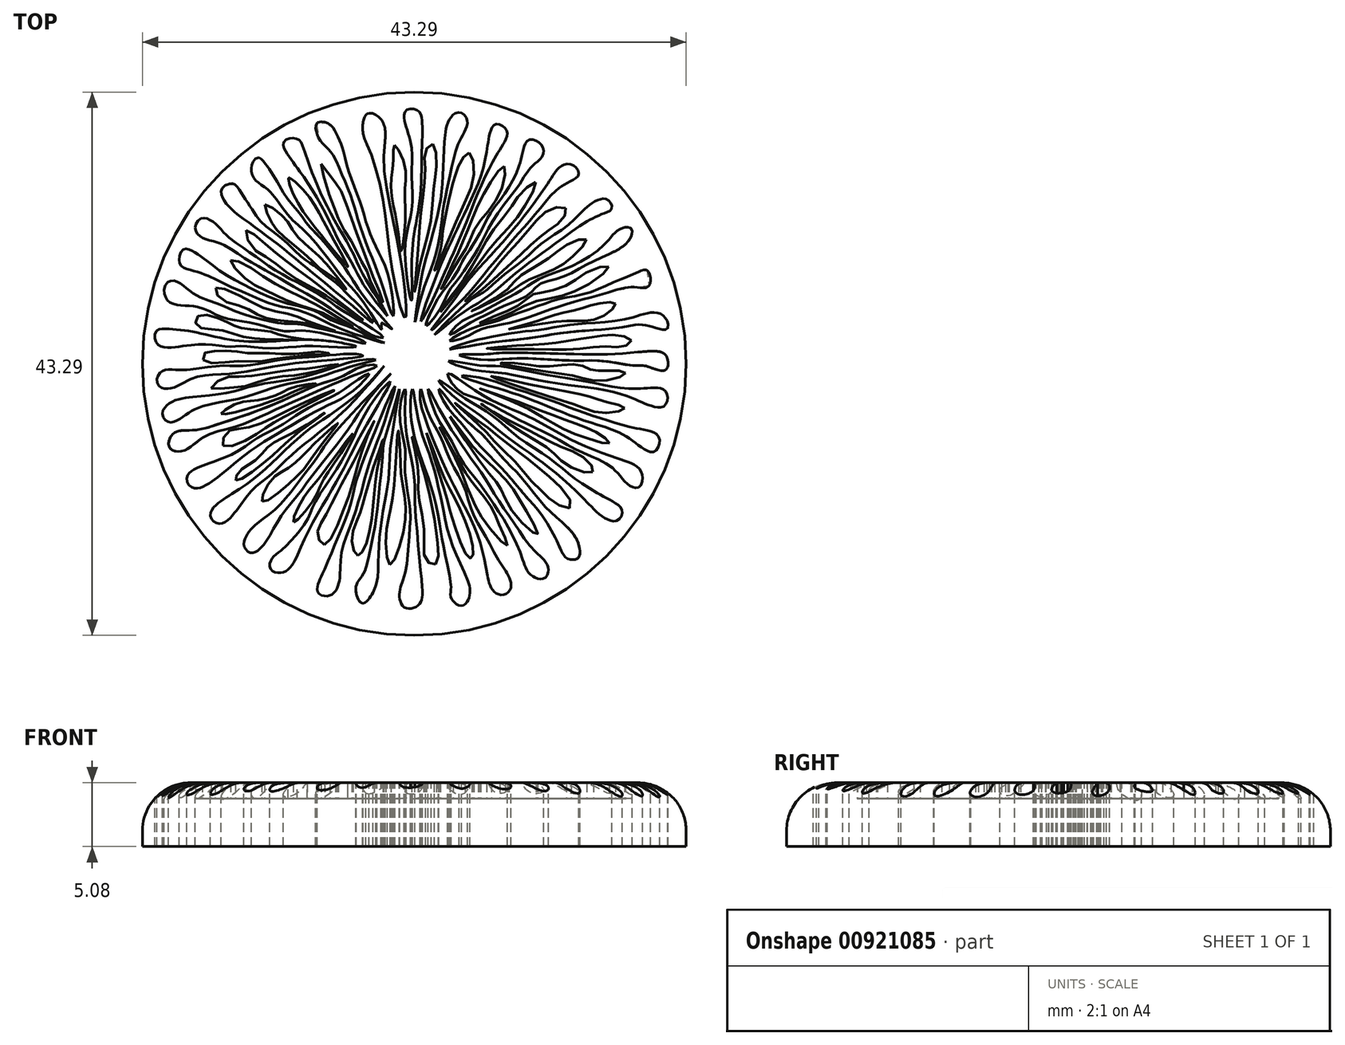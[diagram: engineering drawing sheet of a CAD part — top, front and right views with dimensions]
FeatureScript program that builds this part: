
annotation { "Feature Type Name" : "Feature", "Feature Type Description" : "" }
export const myFeature = defineFeature(function(context is Context, id is Id, definition is map)
    precondition{}
    {
        {
            var Q0;
            Q0=qCreatedBy(makeId("Top.planeOp"),FACE);
            var sketch = newSketch(context, id + "F0", { "sketchPlane" : qUnion([Q0])});
            skFitSpline(sketch, "E0", {"points": [v(-2.98, 20.1) * mm, v(-1.78, 19.44) * mm, v(-1.69, 16.66) * mm, v(-0.95, 11.48) * mm, v(0, 5.92) * mm, v(0, 3.8) * mm, v(-1.04, 7.68) * mm, v(-1.78, 13.42) * mm, v(-2.9, 17.31) * mm, v(-3.36, 18.6) * mm, v(-2.98, 20.1) * mm]});
            skFitSpline(sketch, "E1", {"points": [v(-0.95, 3.98) * mm, v(-1.25, 6.88) * mm, v(-2.23, 9.28) * mm, v(-2.95, 11) * mm, v(-3.54, 12.9) * mm, v(-4.44, 15.37) * mm, v(-4.98, 17.31) * mm, v(-5.57, 18.71) * mm, v(-6.16, 19.34) * mm, v(-7.01, 19.34) * mm, v(-6.83, 18.08) * mm, v(-5.93, 17.09) * mm, v(-5.03, 15.28) * mm, v(-4.17, 13.12) * mm, v(-3.72, 11.54) * mm, v(-2.68, 8.74) * mm, v(-1.78, 6.3) * mm, v(-0.95, 3.98) * mm]});
            skFitSpline(sketch, "E2", {"points": [v(-1.06, 2.92) * mm, v(-2.3, 4.37) * mm, v(-3.72, 6.12) * mm, v(-4.76, 7.75) * mm, v(-5.48, 8.7) * mm, v(-6.6, 10.05) * mm, v(-7.64, 11.13) * mm, v(-8.46, 12.21) * mm, v(-9.45, 13.43) * mm, v(-10.35, 14.97) * mm, v(-11.12, 16.1) * mm, v(-11.7, 16.6) * mm, v(-12.2, 16) * mm, v(-11.98, 14.88) * mm, v(-10.8, 13.93) * mm, v(-9.27, 11.94) * mm, v(-8.14, 10.9) * mm, v(-6.52, 9.06) * mm, v(-4.9, 6.94) * mm, v(-3.36, 5.13) * mm, v(-1.87, 2.92) * mm, v(-1.87, 3.42) * mm, v(-1.06, 2.92) * mm]});
            skFitSpline(sketch, "E3", {"points": [v(-2.55, 3.4) * mm, v(-3.36, 4.5) * mm, v(-4.4, 5.51) * mm, v(-5.3, 6.44) * mm, v(-6.26, 7.17) * mm, v(-7.46, 8.15) * mm, v(-7.98, 8.45) * mm, v(-9.74, 10.1) * mm, v(-11.39, 11.4) * mm, v(-12.33, 12.68) * mm, v(-13.2, 14.03) * mm, v(-13.68, 14.5) * mm, v(-14.56, 14.15) * mm, v(-14.27, 12.98) * mm, v(-12.74, 11.63) * mm, v(-11.35, 10.6) * mm, v(-9.76, 9.38) * mm, v(-8.2, 8.11) * mm, v(-6.61, 6.8) * mm, v(-5.06, 5.5) * mm, v(-3.63, 4.31) * mm, v(-2.55, 3.4) * mm]});
            skFitSpline(sketch, "E4", {"points": [v(-1.71, 2.24) * mm, v(-2.72, 3.03) * mm, v(-4.18, 3.92) * mm, v(-5.54, 4.8) * mm, v(-6.46, 5.47) * mm, v(-7.8, 6.23) * mm, v(-9.22, 6.99) * mm, v(-10.62, 7.8) * mm, v(-11.8, 8.66) * mm, v(-13.05, 9.51) * mm, v(-14.33, 10.51) * mm, v(-15.15, 11.37) * mm, v(-16.19, 11.76) * mm, v(-16.7, 11.06) * mm, v(-16.22, 10.24) * mm, v(-14.7, 9.75) * mm, v(-12.75, 8.57) * mm, v(-10.8, 7.44) * mm, v(-8.74, 6.23) * mm, v(-6.8, 5.13) * mm, v(-3.36, 2.85) * mm, v(-2.32, 2.33) * mm, v(-1.71, 2.24) * mm]});
            skFitSpline(sketch, "E5", {"points": [v(-1.62, 1.82) * mm, v(-2.87, 2.33) * mm, v(-4.02, 2.94) * mm, v(-6.06, 3.73) * mm, v(-7.13, 4.37) * mm, v(-9.5, 5.01) * mm, v(-12.26, 6.17) * mm, v(-14.54, 7.44) * mm, v(-16.13, 8.63) * mm, v(-17.18, 9.27) * mm, v(-17.71, 9.25) * mm, v(-17.93, 8.1) * mm, v(-16.54, 7.48) * mm, v(-14.07, 6.38) * mm, v(-12.34, 5.64) * mm, v(-10.32, 4.83) * mm, v(-8.3, 4.37) * mm, v(-5.9, 3.29) * mm, v(-3.4, 2.33) * mm, v(-1.62, 1.82) * mm]});
            skFitSpline(sketch, "E6", {"points": [v(-3.12, 1.79) * mm, v(-4.11, 2.33) * mm, v(-6.1, 2.81) * mm, v(-7.26, 3.09) * mm, v(-8.49, 3.33) * mm, v(-9.69, 3.36) * mm, v(-11.43, 3.7) * mm, v(-13.6, 4.37) * mm, v(-14.64, 4.84) * mm, v(-16.54, 5.57) * mm, v(-17.63, 6.38) * mm, v(-18.49, 6.79) * mm, v(-19.12, 6.38) * mm, v(-18.8, 5.11) * mm, v(-16.54, 4.7) * mm, v(-14.6, 3.9) * mm, v(-12.1, 3.4) * mm, v(-9.57, 2.76) * mm, v(-7.58, 2.76) * mm, v(-3.12, 1.79) * mm]});
            skFitSpline(sketch, "E7", {"points": [v(-3.89, 1.53) * mm, v(-5.8, 1.94) * mm, v(-8.56, 2.07) * mm, v(-11.06, 1.94) * mm, v(-14.15, 2.12) * mm, v(-17.05, 2.75) * mm, v(-18.87, 2.93) * mm, v(-19.82, 2.75) * mm, v(-19.69, 1.7) * mm, v(-17.69, 1.57) * mm, v(-15.6, 1.7) * mm, v(-14.06, 1.53) * mm, v(-13.06, 1.57) * mm, v(-10.79, 1.4) * mm, v(-8.02, 1.57) * mm, v(-5.43, 1.48) * mm, v(-3.89, 1.53) * mm]});
            skFitSpline(sketch, "E8", {"points": [v(-3.84, 0.94) * mm, v(-5.98, 0.85) * mm, v(-7.97, 0.66) * mm, v(-9.97, 0.48) * mm, v(-12.79, 0) * mm, v(-14.74, 0) * mm, v(-17.83, -0.33) * mm, v(-19.37, -0.43) * mm, v(-19.73, -1.38) * mm, v(-18.82, -1.83) * mm, v(-16.83, -0.97) * mm, v(-13.74, -0.6) * mm, v(-10.1, 0) * mm, v(-6.8, 0.4) * mm, v(-3.36, 0.8) * mm, v(-3.84, 0.94) * mm]});
            skFitSpline(sketch, "E9", {"points": [v(-2.34, 0.48) * mm, v(-3.36, 0.48) * mm, v(-5.3, 0) * mm, v(-8.47, -0.97) * mm, v(-11.92, -1.56) * mm, v(-14.1, -2.15) * mm, v(-16.83, -2.47) * mm, v(-18.73, -2.97) * mm, v(-19.32, -3.88) * mm, v(-18.69, -4.51) * mm, v(-16.83, -3.51) * mm, v(-13.38, -2.65) * mm, v(-9.97, -1.6) * mm, v(-7.06, -0.97) * mm, v(-4.11, 0) * mm, v(-2.34, 0.48) * mm]});
            skFitSpline(sketch, "E10", {"points": [v(-2.24, 0) * mm, v(-3.27, 0) * mm, v(-4.98, -0.84) * mm, v(-6.77, -1.45) * mm, v(-8.63, -2.26) * mm, v(-10.44, -3.08) * mm, v(-12.87, -3.98) * mm, v(-14.99, -4.68) * mm, v(-16.76, -5.13) * mm, v(-18.43, -5.38) * mm, v(-18.76, -6.5) * mm, v(-17.62, -6.76) * mm, v(-16.02, -5.67) * mm, v(-13.44, -4.83) * mm, v(-10.67, -3.67) * mm, v(-7.92, -2.43) * mm, v(-5.54, -1.4) * mm, v(-3.71, -0.62) * mm, v(-2.24, 0) * mm]});
            skFitSpline(sketch, "E11", {"points": [v(-2.87, -0.62) * mm, v(-4.11, -1.35) * mm, v(-5.54, -2.33) * mm, v(-7.53, -3.26) * mm, v(-9.09, -4.23) * mm, v(-10.5, -5.1) * mm, v(-11.95, -5.87) * mm, v(-13.34, -6.82) * mm, v(-15.99, -7.91) * mm, v(-17.38, -8.86) * mm, v(-16.76, -9.77) * mm, v(-13.21, -7.46) * mm, v(-10.05, -5.36) * mm, v(-6.67, -3.4) * mm, v(-4.11, -1.98) * mm, v(-2.87, -0.62) * mm]});
            skFitSpline(sketch, "E12", {"points": [v(-1.66, 0) * mm, v(-2.87, -1.37) * mm, v(-5.54, -3.6) * mm, v(-7.22, -4.75) * mm, v(-8.85, -6.08) * mm, v(-10.6, -7.73) * mm, v(-12.15, -9.08) * mm, v(-14.1, -10.42) * mm, v(-15.29, -11.35) * mm, v(-15.42, -12.2) * mm, v(-14.5, -12.52) * mm, v(-12.43, -10.2) * mm, v(-10.61, -8.6) * mm, v(-8.87, -6.95) * mm, v(-4.66, -3.4) * mm, v(-1.66, 0) * mm]});
            skFitSpline(sketch, "E13", {"points": [v(-1.12, -0.62) * mm, v(-2.72, -2.42) * mm, v(-4.58, -5.15) * mm, v(-6.87, -8.06) * mm, v(-8.6, -10.38) * mm, v(-10.1, -12.35) * mm, v(-11.1, -14.05) * mm, v(-12.2, -14.91) * mm, v(-12.81, -14.34) * mm, v(-12.18, -12.93) * mm, v(-10.24, -11.34) * mm, v(-8.39, -9.12) * mm, v(-6.98, -7.26) * mm, v(-5.54, -5.27) * mm, v(-1.12, -0.62) * mm]});
            skFitSpline(sketch, "E14", {"points": [v(-1.18, -1.25) * mm, v(-2.72, -3.06) * mm, v(-4.11, -5.73) * mm, v(-5.54, -8.37) * mm, v(-7.29, -11.11) * mm, v(-7.87, -12.41) * mm, v(-9.9, -14.73) * mm, v(-10.5, -15.24) * mm, v(-10.73, -16.16) * mm, v(-9.6, -16.42) * mm, v(-7.98, -13.76) * mm, v(-5.23, -8.84) * mm, v(-3.4, -5.3) * mm, v(-1.18, -1.25) * mm]});
            skFitSpline(sketch, "E15", {"points": [v(-0.82, -1.63) * mm, v(-1.77, -3.7) * mm, v(-2.87, -6.38) * mm, v(-3.84, -9.05) * mm, v(-4.42, -11.34) * mm, v(-5.48, -14.02) * mm, v(-6.57, -16.58) * mm, v(-6.94, -18.07) * mm, v(-5.92, -18.28) * mm, v(-5.22, -17.08) * mm, v(-5.07, -15.02) * mm, v(-4.22, -12.4) * mm, v(-3.36, -9.57) * mm, v(-2.87, -7.83) * mm, v(-1.72, -4.67) * mm, v(-0.82, -1.63) * mm]});
            skFitSpline(sketch, "E16", {"points": [v(-0.44, -1.84) * mm, v(-1.16, -4.36) * mm, v(-1.68, -6.16) * mm, v(-1.88, -8.25) * mm, v(-2.12, -10.45) * mm, v(-2.34, -12.46) * mm, v(-2.87, -15.13) * mm, v(-3.36, -16.66) * mm, v(-3.84, -17.34) * mm, v(-3.84, -18.33) * mm, v(-3.36, -18.92) * mm, v(-2.35, -17.59) * mm, v(-2.12, -15.13) * mm, v(-1.8, -11.82) * mm, v(-1.32, -9.02) * mm, v(-1.13, -6.23) * mm, v(-0.44, -1.84) * mm]});
            skFitSpline(sketch, "E17", {"points": [v(0, -1.84) * mm, v(-0.44, -3.73) * mm, v(0, -6.58) * mm, v(0, -8.53) * mm, v(0.4, -11.3) * mm, v(0.3, -13.9) * mm, v(0, -16.49) * mm, v(-0.44, -18.2) * mm, v(0, -19.29) * mm, v(1.1, -19.04) * mm, v(1.38, -17.91) * mm, v(1.12, -15.23) * mm, v(0.97, -13.27) * mm, v(0.8, -11.3) * mm, v(0.72, -8.73) * mm, v(0, -4.3) * mm, v(0, -1.84) * mm]});
            skFitSpline(sketch, "E18", {"points": [v(0.59, -1.84) * mm, v(0.43, -3.4) * mm, v(0.8, -5.84) * mm, v(1.42, -7.78) * mm, v(2.27, -10.28) * mm, v(2.81, -12.95) * mm, v(3.13, -14.77) * mm, v(3.66, -17.6) * mm, v(3.68, -18.52) * mm, v(4.5, -19.12) * mm, v(5.16, -18.12) * mm, v(4.45, -15.88) * mm, v(3.54, -13.62) * mm, v(3.03, -11.36) * mm, v(2.66, -9.66) * mm, v(2.12, -7.61) * mm, v(1.27, -5.15) * mm, v(0.83, -3.03) * mm, v(0.59, -1.84) * mm]});
            skFitSpline(sketch, "E19", {"points": [v(1.26, -1.84) * mm, v(1.2, -2.62) * mm, v(2.02, -5.32) * mm, v(3, -7.68) * mm, v(4.07, -9.92) * mm, v(5.22, -12.2) * mm, v(6.03, -14.3) * mm, v(6.48, -16.34) * mm, v(7.06, -17.98) * mm, v(7.96, -18.21) * mm, v(8.45, -17.44) * mm, v(7.36, -15.32) * mm, v(6.3, -13.37) * mm, v(5.42, -11.82) * mm, v(4.7, -9.66) * mm, v(3.65, -7.59) * mm, v(2.72, -5.45) * mm, v(1.65, -3.25) * mm, v(1.26, -1.84) * mm]});
            skFitSpline(sketch, "E20", {"points": [v(1.83, -1.84) * mm, v(2.49, -3.97) * mm, v(3.54, -5.71) * mm, v(4.53, -7.57) * mm, v(5.83, -9.26) * mm, v(7.04, -10.98) * mm, v(8.36, -13.13) * mm, v(9.32, -15.31) * mm, v(9.94, -16.59) * mm, v(11.02, -16.97) * mm, v(11.4, -16.06) * mm, v(10.2, -14.63) * mm, v(8.77, -12.68) * mm, v(7.4, -10.65) * mm, v(6.24, -8.77) * mm, v(5, -7) * mm, v(3.72, -5.12) * mm, v(2.68, -3.33) * mm, v(1.83, -1.84) * mm]});
            skFitSpline(sketch, "E21", {"points": [v(2.68, -1.84) * mm, v(3.12, -2.93) * mm, v(4.5, -4.63) * mm, v(5.66, -6.05) * mm, v(7.24, -7.7) * mm, v(8.35, -8.9) * mm, v(9.8, -10.6) * mm, v(10.66, -11.58) * mm, v(11.62, -13.06) * mm, v(12.34, -14.52) * mm, v(12.89, -15.33) * mm, v(13.77, -15.3) * mm, v(13.7, -13.9) * mm, v(12.45, -12.42) * mm, v(10.97, -11) * mm, v(9.13, -8.75) * mm, v(7.59, -7.15) * mm, v(6.35, -5.68) * mm, v(4.28, -3.73) * mm, v(2.68, -1.84) * mm]});
            skFitSpline(sketch, "E22", {"points": [v(2.68, -1.14) * mm, v(3.68, -2.3) * mm, v(5.76, -3.79) * mm, v(7.96, -5.54) * mm, v(10.23, -7.18) * mm, v(12.18, -8.7) * mm, v(14.33, -10.7) * mm, v(15.9, -12.13) * mm, v(16.95, -12.3) * mm, v(17.28, -11.51) * mm, v(16.1, -10.58) * mm, v(13.59, -9.04) * mm, v(11.64, -7.48) * mm, v(8.92, -5.62) * mm, v(6.83, -3.87) * mm, v(4.7, -2.54) * mm, v(2.68, -1.14) * mm]});
            skFitSpline(sketch, "E23", {"points": [v(3.4, -0.62) * mm, v(5.38, -1.84) * mm, v(7.94, -3.22) * mm, v(10.12, -4.19) * mm, v(12.3, -5.4) * mm, v(14.75, -6.57) * mm, v(17.29, -7.5) * mm, v(18.75, -8.38) * mm, v(18.74, -9.57) * mm, v(17.97, -9.6) * mm, v(16.46, -8.1) * mm, v(14.22, -6.96) * mm, v(11.53, -5.52) * mm, v(8.8, -4.15) * mm, v(5.96, -2.7) * mm, v(4.12, -1.84) * mm, v(3.4, -0.62) * mm]});
            skFitSpline(sketch, "E24", {"points": [v(4.48, -0.82) * mm, v(7.1, -1.71) * mm, v(9.62, -2.54) * mm, v(12.5, -3.69) * mm, v(15.04, -4.62) * mm, v(17.69, -5.68) * mm, v(19.8, -6.85) * mm, v(20.21, -5.7) * mm, v(18.49, -5) * mm, v(16.23, -4.39) * mm, v(13.53, -3.48) * mm, v(10.99, -2.54) * mm, v(8.83, -1.84) * mm, v(6.1, -0.97) * mm, v(4.48, -0.82) * mm]});
            skFitSpline(sketch, "E25", {"points": [v(3.45, 0.38) * mm, v(4.95, -0.21) * mm, v(7.97, -0.62) * mm, v(11.09, -1.24) * mm, v(15.34, -1.84) * mm, v(18, -2.54) * mm, v(20.48, -3.29) * mm, v(20.9, -2.54) * mm, v(20.51, -1.84) * mm, v(18.17, -1.84) * mm, v(14.93, -1.33) * mm, v(10.76, -0.62) * mm, v(7.29, 0) * mm, v(6.21, 0) * mm, v(3.45, 0.38) * mm]});
            skFitSpline(sketch, "E26", {"points": [v(4.3, 0.86) * mm, v(6, 0.49) * mm, v(7.96, 0.54) * mm, v(10.09, 0.58) * mm, v(12, 0.47) * mm, v(13.84, 0.41) * mm, v(16.04, 0.35) * mm, v(18.36, 0) * mm, v(19.1, 0) * mm, v(20.73, -0.34) * mm, v(20.84, 0.69) * mm, v(20.17, 1.14) * mm, v(18.16, 1.05) * mm, v(15.9, 0.9) * mm, v(13.22, 0.94) * mm, v(10.62, 1) * mm, v(7.7, 1.03) * mm, v(6.2, 0.92) * mm, v(4.3, 0.86) * mm]});
            skFitSpline(sketch, "E27", {"points": [v(3.54, 1.34) * mm, v(6.37, 1.79) * mm, v(9.8, 2.19) * mm, v(12.45, 2.61) * mm, v(15.42, 2.88) * mm, v(17.44, 3.1) * mm, v(19.19, 3.24) * mm, v(20.85, 2.92) * mm, v(20.72, 3.83) * mm, v(19.6, 4.24) * mm, v(17.85, 3.79) * mm, v(14.84, 3.41) * mm, v(12.7, 3.2) * mm, v(10.76, 2.87) * mm, v(9.14, 2.7) * mm, v(6.76, 2.29) * mm, v(5.14, 1.9) * mm, v(3.54, 1.34) * mm]});
            skFitSpline(sketch, "E28", {"points": [v(3.54, 2) * mm, v(4.68, 2.22) * mm, v(6.12, 2.95) * mm, v(7.5, 3.25) * mm, v(9.8, 3.86) * mm, v(11.68, 4.53) * mm, v(13.75, 5.18) * mm, v(15.93, 5.77) * mm, v(18.17, 6.28) * mm, v(19.42, 6.36) * mm, v(19.33, 7.58) * mm, v(18.45, 7.41) * mm, v(16.47, 6.6) * mm, v(14.5, 5.79) * mm, v(12.5, 5.37) * mm, v(10.76, 4.82) * mm, v(8.62, 4.05) * mm, v(6.97, 3.47) * mm, v(5.22, 2.94) * mm, v(3.54, 2) * mm]});
            skFitSpline(sketch, "E29", {"points": [v(3.54, 2.48) * mm, v(5.22, 3.45) * mm, v(6.8, 4.23) * mm, v(8.19, 4.91) * mm, v(9.8, 5.64) * mm, v(10.76, 6.52) * mm, v(12.53, 7.08) * mm, v(14.37, 8.02) * mm, v(16.28, 8.92) * mm, v(17.83, 10.02) * mm, v(17.97, 10.97) * mm, v(16.94, 10.78) * mm, v(15.91, 9.7) * mm, v(13.23, 7.92) * mm, v(10.76, 6.97) * mm, v(9.37, 6.1) * mm, v(7.69, 5.17) * mm, v(5.88, 4.18) * mm, v(4.37, 3.43) * mm, v(3.54, 2.48) * mm]});
            skFitSpline(sketch, "E30", {"points": [v(2.34, 2.47) * mm, v(3.54, 3.45) * mm, v(5.22, 4.63) * mm, v(7, 5.83) * mm, v(8.5, 7.13) * mm, v(10.2, 8.45) * mm, v(11.92, 9.72) * mm, v(14.3, 11.38) * mm, v(15.85, 12.16) * mm, v(16.46, 12.55) * mm, v(16.08, 13.26) * mm, v(14.72, 12.84) * mm, v(13.03, 11.26) * mm, v(11.03, 9.86) * mm, v(9.4, 8.42) * mm, v(7.67, 7.08) * mm, v(6.34, 5.92) * mm, v(5.22, 5.25) * mm, v(2.34, 2.47) * mm]});
            skFitSpline(sketch, "E31", {"points": [v(2.07, 2.81) * mm, v(3.55, 4.23) * mm, v(5.17, 5.94) * mm, v(6.96, 8.1) * mm, v(8.95, 10.46) * mm, v(10.76, 12.54) * mm, v(12.43, 14.28) * mm, v(13.82, 15.25) * mm, v(13.34, 16) * mm, v(12.38, 15.89) * mm, v(11.27, 14.39) * mm, v(9.8, 12.37) * mm, v(8.36, 10.54) * mm, v(6.38, 8.32) * mm, v(4.82, 6.53) * mm, v(3.54, 4.78) * mm, v(2.07, 2.81) * mm]});
            skFitSpline(sketch, "E32", {"points": [v(1.67, 3.21) * mm, v(2.65, 4.3) * mm, v(3.54, 6.02) * mm, v(4.3, 7.01) * mm, v(5.63, 9.04) * mm, v(6.34, 10.35) * mm, v(7.5, 12.35) * mm, v(9, 14.3) * mm, v(10, 15.78) * mm, v(10.93, 16.72) * mm, v(10.84, 17.63) * mm, v(9.83, 17.98) * mm, v(9.18, 16.27) * mm, v(8.57, 14.79) * mm, v(7.83, 13.56) * mm, v(6.9, 12.34) * mm, v(6.43, 11.47) * mm, v(5.4, 9.6) * mm, v(4.62, 8.46) * mm, v(4.3, 7.79) * mm, v(3.54, 6.6) * mm, v(2.53, 5.2) * mm, v(1.67, 3.21) * mm]});
            skFitSpline(sketch, "E33", {"points": [v(1.25, 3.53) * mm, v(2.53, 6) * mm, v(3.54, 8.32) * mm, v(4.72, 11.05) * mm, v(5.77, 13.73) * mm, v(7.2, 16.65) * mm, v(7.93, 17.85) * mm, v(8.08, 18.76) * mm, v(7.3, 19.27) * mm, v(6.76, 18.56) * mm, v(6.27, 15.94) * mm, v(4.82, 12.3) * mm, v(3.54, 9.6) * mm, v(2.53, 7.27) * mm, v(1.25, 3.53) * mm]});
            skFitSpline(sketch, "E34", {"points": [v(0.8, 3.5) * mm, v(1.34, 5.7) * mm, v(2.53, 9.13) * mm, v(3.04, 12.5) * mm, v(3.54, 14.97) * mm, v(4.3, 17.86) * mm, v(4.97, 19.5) * mm, v(4.3, 20.2) * mm, v(3.54, 19.64) * mm, v(3.14, 17.86) * mm, v(2.97, 14.58) * mm, v(2.53, 11.7) * mm, v(1.56, 8.2) * mm, v(1.1, 5.88) * mm, v(0.8, 3.5) * mm]});
            skFitSpline(sketch, "E35", {"points": [v(0.53, 7.45) * mm, v(0.7, 10.36) * mm, v(1.2, 13.45) * mm, v(1.34, 17.14) * mm, v(1.34, 19.67) * mm, v(0.92, 20.4) * mm, v(0, 20.25) * mm, v(0.44, 17.82) * mm, v(0.53, 15.5) * mm, v(0.54, 12.5) * mm, v(0, 9.33) * mm, v(0.51, 5.2) * mm, v(0.53, 7.45) * mm]});
            skFitSpline(sketch, "E36", {"points": [v(-1.4, 3.97) * mm, v(-2.28, 5.52) * mm, v(-3.41, 7.4) * mm, v(-4.27, 9.21) * mm, v(-5.56, 11.48) * mm, v(-6.67, 13.68) * mm, v(-7.5, 15.64) * mm, v(-8.06, 17.3) * mm, v(-8.62, 18.1) * mm, v(-9.65, 17.85) * mm, v(-9.19, 16.61) * mm, v(-8.06, 15.03) * mm, v(-6.63, 12.7) * mm, v(-5.2, 9.84) * mm, v(-4.23, 8.17) * mm, v(-3.45, 6.69) * mm, v(-2.46, 5.28) * mm, v(-1.4, 3.97) * mm]});
            skCircle(sketch, "E37", {"center": v(0.73, 0.16) * mm, "radius": 21.65 * mm});
            skPoint(sketch, "E37.first.point", {"position": v(0, 21.8) * mm});
            skPoint(sketch, "E37.second.point", {"position": v(22.38, 0) * mm});
            skPoint(sketch, "E37.third.point", {"position": v(-2.4, -21.26) * mm});
            skSolve(sketch);
        }
        {
            var Q0;
            Q0=makeQuery(id+"F0.imprint","IMPRINT",FACE,{"disambiguationData":[TD([[makeQuery(id+"F0.imprint","IMPRINT",EDGE,{"derivedFrom":sQuery(id+"F0.wireOp",EDGE,"E0")}),1.0]])]});
            var sketch = newSketch(context, id + "F1", { "sketchPlane" : qUnion([Q0])});
            skFitSpline(sketch, "E38", {"points": [v(-9.26, 14.97) * mm, v(-9.03, 13.97) * mm, v(-7.84, 11.92) * mm, v(-6.54, 10.24) * mm, v(-5.38, 8.83) * mm, v(-4.56, 7.9) * mm, v(-5.64, 9.98) * mm, v(-6.83, 12.18) * mm, v(-8.03, 13.93) * mm, v(-9.26, 14.97) * mm]});
            skFitSpline(sketch, "E39", {"points": [v(-6.68, 16.08) * mm, v(-5.95, 15.1) * mm, v(-5.26, 14.22) * mm, v(-4.6, 12.64) * mm, v(-3.84, 10.5) * mm, v(-3.01, 8.32) * mm, v(-2.2, 6.27) * mm, v(-1.78, 5.07) * mm, v(-2.64, 6.45) * mm, v(-2.98, 7.46) * mm, v(-3.58, 8.54) * mm, v(-4.12, 9.67) * mm, v(-4.84, 10.8) * mm, v(-5.54, 12.32) * mm, v(-6.1, 13.87) * mm, v(-6.68, 16.08) * mm]});
            skFitSpline(sketch, "E40", {"points": [v(-3.91, 16.99) * mm, v(-3.3, 15.87) * mm, v(-2.46, 13.26) * mm, v(-1.85, 10.97) * mm, v(-1.56, 8.62) * mm, v(-0.9, 4.81) * mm, v(-1.85, 8.66) * mm, v(-2.6, 10.8) * mm, v(-2.93, 12.35) * mm, v(-3.59, 14.3) * mm, v(-4.02, 15.72) * mm, v(-3.91, 16.99) * mm]});
            skFitSpline(sketch, "E41", {"points": [v(-0.83, 17.57) * mm, v(-0.94, 16.37) * mm, v(-1.12, 14.63) * mm, v(-0.9, 12.68) * mm, v(-0.54, 10.68) * mm, v(-0.32, 9.13) * mm, v(0, 11.37) * mm, v(0, 14.1) * mm, v(0, 15.87) * mm, v(-0.83, 17.57) * mm]});
            skFitSpline(sketch, "E42", {"points": [v(2.21, 17.68) * mm, v(1.63, 17.13) * mm, v(1.6, 15.68) * mm, v(1.34, 12.86) * mm, v(1.13, 10.5) * mm, v(0.98, 8.55) * mm, v(0.76, 5.9) * mm, v(1.27, 8.44) * mm, v(2, 11.23) * mm, v(2.32, 14.42) * mm, v(2.5, 16.08) * mm, v(2.21, 17.68) * mm]});
            skFitSpline(sketch, "E43", {"points": [v(5.11, 16.99) * mm, v(4.42, 16.26) * mm, v(3.99, 15.1) * mm, v(3.66, 14.02) * mm, v(3.44, 12.93) * mm, v(3.12, 11.48) * mm, v(2.94, 10) * mm, v(2.72, 8.8) * mm, v(2.32, 7.46) * mm, v(3.66, 10.54) * mm, v(4.71, 12.93) * mm, v(5.47, 15.25) * mm, v(5.11, 16.99) * mm]});
            skFitSpline(sketch, "E44", {"points": [v(7.9, 15.9) * mm, v(7.1, 15.07) * mm, v(5.94, 13.11) * mm, v(5.11, 11.12) * mm, v(4.35, 9.3) * mm, v(3.34, 7.1) * mm, v(2.83, 6.01) * mm, v(4.24, 8.4) * mm, v(5.04, 9.7) * mm, v(5.65, 11.08) * mm, v(6.7, 12.42) * mm, v(7.8, 14.42) * mm, v(7.9, 15.9) * mm]});
            skFitSpline(sketch, "E45", {"points": [v(10.4, 14.63) * mm, v(9.28, 13.8) * mm, v(8.52, 12.75) * mm, v(7.14, 10.97) * mm, v(6.09, 9.27) * mm, v(4.9, 7.2) * mm, v(3.99, 5.94) * mm, v(3.48, 5.32) * mm, v(2.83, 4.3) * mm, v(5.44, 7.57) * mm, v(7, 9.63) * mm, v(8.63, 11.45) * mm, v(9.78, 13.15) * mm, v(10.4, 14.63) * mm]});
            skFitSpline(sketch, "E46", {"points": [v(12.8, 12.57) * mm, v(11.6, 12.5) * mm, v(10.26, 11.34) * mm, v(8.66, 9.49) * mm, v(7.36, 8) * mm, v(6.05, 6.45) * mm, v(4.78, 5.14) * mm, v(5.84, 5.83) * mm, v(7.65, 7.46) * mm, v(8.92, 8.58) * mm, v(10.33, 9.92) * mm, v(11.56, 10.87) * mm, v(12.61, 11.8) * mm, v(12.8, 12.57) * mm]});
            skFitSpline(sketch, "E47", {"points": [v(14.44, 10.06) * mm, v(13.12, 9.78) * mm, v(11.53, 8.65) * mm, v(10.16, 7.8) * mm, v(8.9, 6.9) * mm, v(7.62, 5.69) * mm, v(5.32, 4.37) * mm, v(8.42, 5.92) * mm, v(9.64, 6.77) * mm, v(11.8, 7.66) * mm, v(13.4, 8.79) * mm, v(14.44, 10.06) * mm]});
            skFitSpline(sketch, "E48", {"points": [v(16.23, 7.9) * mm, v(14.58, 7.52) * mm, v(13.03, 6.49) * mm, v(11.1, 5.87) * mm, v(10.16, 5.69) * mm, v(9.27, 4.98) * mm, v(7.67, 4.18) * mm, v(5.84, 3.34) * mm, v(7.76, 3.9) * mm, v(10.2, 5.08) * mm, v(12.18, 5.5) * mm, v(14.49, 6.44) * mm, v(16.23, 7.9) * mm]});
            skFitSpline(sketch, "E49", {"points": [v(16.74, 4.93) * mm, v(15.47, 4.98) * mm, v(13.78, 4.51) * mm, v(11.85, 4.04) * mm, v(10.07, 3.43) * mm, v(8.28, 2.91) * mm, v(11.34, 3.43) * mm, v(13.73, 3.57) * mm, v(15.57, 3.85) * mm, v(16.74, 4.93) * mm]});
            skFitSpline(sketch, "E50", {"points": [v(17.54, -0.57) * mm, v(16.27, -0.38) * mm, v(14.91, -0.33) * mm, v(13.73, 0.1) * mm, v(11.48, -0.05) * mm, v(9.36, 0.14) * mm, v(7.53, 0.23) * mm, v(11, -0.42) * mm, v(13.6, -0.85) * mm, v(15.9, -1.18) * mm, v(17.54, -0.57) * mm]});
            skFitSpline(sketch, "E51", {"points": [v(18.01, 2.02) * mm, v(16.88, 2.44) * mm, v(15.38, 2.35) * mm, v(13.69, 2.11) * mm, v(11.56, 1.78) * mm, v(9.4, 1.64) * mm, v(6.5, 1.36) * mm, v(10.26, 1.31) * mm, v(13.55, 1.31) * mm, v(15.9, 1.55) * mm, v(17.4, 1.55) * mm, v(18.01, 2.02) * mm]});
            skFitSpline(sketch, "E52", {"points": [v(17.5, -3.39) * mm, v(16.04, -2.87) * mm, v(14.68, -2.45) * mm, v(12.47, -1.98) * mm, v(9.13, -1.32) * mm, v(6.87, -0.85) * mm, v(10.59, -2.16) * mm, v(13.78, -3.2) * mm, v(15.85, -3.76) * mm, v(17.5, -3.39) * mm]});
            skFitSpline(sketch, "E53", {"points": [v(16.27, -6.16) * mm, v(15.52, -5.46) * mm, v(13.97, -4.75) * mm, v(11.8, -3.95) * mm, v(9.64, -3.1) * mm, v(7.76, -2.45) * mm, v(5.88, -1.79) * mm, v(9.4, -3.25) * mm, v(12.14, -4.8) * mm, v(14.4, -5.74) * mm, v(16.27, -6.16) * mm]});
            skFitSpline(sketch, "E54", {"points": [v(14.96, -8.46) * mm, v(14.4, -7.43) * mm, v(12.18, -6.35) * mm, v(10.26, -5.36) * mm, v(8.38, -4.42) * mm, v(7.1, -3.72) * mm, v(6.03, -3.01) * mm, v(9.17, -5.22) * mm, v(11.62, -6.77) * mm, v(12.98, -7.95) * mm, v(14.96, -8.46) * mm]});
            skFitSpline(sketch, "E55", {"points": [v(13.1, -11.34) * mm, v(13.1, -10.62) * mm, v(11.5, -8.88) * mm, v(10.3, -7.85) * mm, v(7.57, -5.74) * mm, v(6.28, -4.71) * mm, v(4.88, -3.7) * mm, v(3.82, -2.86) * mm, v(6.25, -5.05) * mm, v(7.23, -6.15) * mm, v(8.78, -7.67) * mm, v(9.84, -8.95) * mm, v(11.02, -10.13) * mm, v(11.89, -10.88) * mm, v(13.1, -11.34) * mm]});
            skFitSpline(sketch, "E56", {"points": [v(8.14, -14.33) * mm, v(7.46, -12.62) * mm, v(6.89, -11.3) * mm, v(5.75, -9.79) * mm, v(5, -8.76) * mm, v(3.97, -7.06) * mm, v(2.76, -4.9) * mm, v(4.35, -8.12) * mm, v(4.88, -9.48) * mm, v(5.41, -10.77) * mm, v(6.59, -12.78) * mm, v(8.14, -14.33) * mm]});
            skFitSpline(sketch, "E57", {"points": [v(2.42, -15.8) * mm, v(2.57, -13.91) * mm, v(2.23, -11.64) * mm, v(1.74, -9.37) * mm, v(1.25, -7.63) * mm, v(0.53, -5.55) * mm, v(1.02, -8.08) * mm, v(1.06, -10.13) * mm, v(1.51, -13.2) * mm, v(1.67, -15.46) * mm, v(2.42, -15.8) * mm]});
            skFitSpline(sketch, "E58", {"points": [v(-1.21, -15.84) * mm, v(-0.3, -13.97) * mm, v(0.03, -11.05) * mm, v(-0.3, -8.8) * mm, v(-0.4, -6.79) * mm, v(-0.54, -5.16) * mm, v(-0.78, -8.51) * mm, v(-1.17, -11.48) * mm, v(-1.5, -13.4) * mm, v(-1.21, -15.84) * mm]});
            skFitSpline(sketch, "E59", {"points": [v(-3.75, -15.12) * mm, v(-2.99, -13.83) * mm, v(-2.46, -10.38) * mm, v(-2.03, -7.27) * mm, v(-1.7, -5.78) * mm, v(-2.99, -9.61) * mm, v(-3.56, -11.67) * mm, v(-4.23, -13.78) * mm, v(-3.75, -15.12) * mm]});
            skFitSpline(sketch, "E60", {"points": [v(-6.44, -14.26) * mm, v(-4.9, -11.53) * mm, v(-4, -8.75) * mm, v(-3.13, -5.92) * mm, v(-2.46, -4.39) * mm, v(-4.19, -7.8) * mm, v(-5.34, -10) * mm, v(-6.4, -12) * mm, v(-6.97, -13.4) * mm, v(-6.44, -14.26) * mm]});
            skFitSpline(sketch, "E61", {"points": [v(-8.88, -12.44) * mm, v(-7.5, -11) * mm, v(-6.58, -9.23) * mm, v(-5.43, -7.46) * mm, v(-4.14, -5.35) * mm, v(-6, -7.84) * mm, v(-7.16, -9.33) * mm, v(-8.16, -10.62) * mm, v(-8.88, -12.44) * mm]});
            skFitSpline(sketch, "E62", {"points": [v(-11.37, -10.81) * mm, v(-9.46, -9.61) * mm, v(-7.88, -7.98) * mm, v(-6.82, -6.5) * mm, v(-5.34, -4.58) * mm, v(-6.73, -5.73) * mm, v(-8.21, -7.22) * mm, v(-9.4, -8.22) * mm, v(-10.6, -9.04) * mm, v(-11.37, -10.81) * mm]});
            skFitSpline(sketch, "E63", {"points": [v(-13.48, -9.13) * mm, v(-11.37, -7.84) * mm, v(-9.7, -6.35) * mm, v(-8.3, -5.16) * mm, v(-6.4, -3.77) * mm, v(-9.03, -5.4) * mm, v(-10.85, -6.4) * mm, v(-12, -7.6) * mm, v(-13.15, -8.37) * mm, v(-13.48, -9.13) * mm]});
            skFitSpline(sketch, "E64", {"points": [v(-14.49, -6.35) * mm, v(-12.29, -5.73) * mm, v(-10.6, -4.63) * mm, v(-8.79, -3.62) * mm, v(-7.2, -2.76) * mm, v(-5.53, -1.9) * mm, v(-8.3, -3.05) * mm, v(-10.22, -4) * mm, v(-12.72, -4.96) * mm, v(-14.1, -5.25) * mm, v(-14.49, -6.35) * mm]});
            skFitSpline(sketch, "E65", {"points": [v(-14.63, -3.81) * mm, v(-12.9, -3.53) * mm, v(-9.75, -2.47) * mm, v(-8.02, -1.7) * mm, v(-7.06, -1.42) * mm, v(-8.83, -1.7) * mm, v(-10.03, -2.23) * mm, v(-11.8, -2.76) * mm, v(-13.24, -2.95) * mm, v(-14.63, -3.81) * mm]});
            skFitSpline(sketch, "E66", {"points": [v(-15.44, -1.77) * mm, v(-14.14, -1.74) * mm, v(-12.62, -1.62) * mm, v(-10.8, -1) * mm, v(-9.18, -0.81) * mm, v(-7.73, -0.6) * mm, v(-6.46, -0.28) * mm, v(-5.31, 0.12) * mm, v(-6.95, -0.1) * mm, v(-7.88, -0.22) * mm, v(-8.69, -0.28) * mm, v(-9.9, -0.44) * mm, v(-11.5, -0.72) * mm, v(-13.37, -0.87) * mm, v(-14.45, -0.97) * mm, v(-15.44, -1.77) * mm]});
            skFitSpline(sketch, "E67", {"points": [v(3.59, -4.05) * mm, v(5.18, -6.13) * mm, v(6.27, -7.33) * mm, v(8.2, -9.31) * mm, v(9.54, -11.4) * mm, v(10.54, -13.43) * mm, v(8.7, -11.8) * mm, v(7.56, -9.7) * mm, v(6.37, -8.17) * mm, v(3.59, -4.05) * mm]});
            skFitSpline(sketch, "E68", {"points": [v(-16.1, 0.46) * mm, v(-15, 0.21) * mm, v(-13.24, 0.37) * mm, v(-11.63, 0.34) * mm, v(-10.3, 0.55) * mm, v(-8.9, 0.7) * mm, v(-7.14, 0.9) * mm, v(-6, 0.96) * mm, v(-6.8, 1.14) * mm, v(-8, 1.02) * mm, v(-9.9, 0.96) * mm, v(-11.26, 1.02) * mm, v(-12.5, 1.02) * mm, v(-13.61, 1.17) * mm, v(-15, 1.17) * mm, v(-15.94, 1.02) * mm, v(-16.1, 0.46) * mm]});
            skFitSpline(sketch, "E69", {"points": [v(-16.57, 3.2) * mm, v(-14.96, 2.9) * mm, v(-13.04, 2.36) * mm, v(-11.1, 2.12) * mm, v(-9.64, 2.08) * mm, v(-7.78, 2.08) * mm, v(-9.46, 2.33) * mm, v(-10.69, 2.72) * mm, v(-12.48, 2.93) * mm, v(-13.6, 3.2) * mm, v(-14.75, 3.73) * mm, v(-16.47, 3.98) * mm, v(-16.57, 3.2) * mm]});
            skFitSpline(sketch, "E70", {"points": [v(1.7, -5.34) * mm, v(3, -8.62) * mm, v(4.48, -11.64) * mm, v(5.42, -15.02) * mm, v(5.13, -15.32) * mm, v(3.79, -12.24) * mm, v(3.24, -10.3) * mm, v(1.7, -5.34) * mm]});
            skFitSpline(sketch, "E71", {"points": [v(-15.07, 6.22) * mm, v(-13.08, 5.52) * mm, v(-10.98, 4.53) * mm, v(-8.94, 4.04) * mm, v(-7.33, 3.4) * mm, v(-5.43, 2.73) * mm, v(-7.53, 3.3) * mm, v(-8.7, 3.5) * mm, v(-10.29, 3.66) * mm, v(-11.62, 4) * mm, v(-12.85, 4.7) * mm, v(-14.6, 5.3) * mm, v(-15.07, 6.22) * mm]});
            skFitSpline(sketch, "E72", {"points": [v(-13.88, 8.4) * mm, v(-12.9, 8.15) * mm, v(-10.8, 6.81) * mm, v(-8.62, 5.66) * mm, v(-6.35, 4.47) * mm, v(-4.94, 3.6) * mm, v(-4.14, 3.1) * mm, v(-5.64, 3.73) * mm, v(-6.63, 4.26) * mm, v(-8.66, 4.92) * mm, v(-10.13, 5.55) * mm, v(-11.64, 6.25) * mm, v(-13.04, 7.23) * mm, v(-13.88, 8.4) * mm]});
            skFitSpline(sketch, "E73", {"points": [v(-12.65, 10.77) * mm, v(-11.6, 10.1) * mm, v(-9.95, 8.74) * mm, v(-8.1, 7.34) * mm, v(-6.56, 6.15) * mm, v(-4.84, 4.82) * mm, v(-3.37, 3.66) * mm, v(-5.57, 5.11) * mm, v(-6.73, 5.87) * mm, v(-8.1, 6.6) * mm, v(-9.5, 7.51) * mm, v(-10.97, 8.6) * mm, v(-12.2, 9.48) * mm, v(-12.65, 10.77) * mm]});
            skFitSpline(sketch, "E74", {"points": [v(-11.14, 12.84) * mm, v(-10.76, 11.68) * mm, v(-10.23, 10.84) * mm, v(-9, 9.76) * mm, v(-7.6, 8.57) * mm, v(-6.66, 7.65) * mm, v(-5.57, 6.95) * mm, v(-4.6, 5.97) * mm, v(-6.03, 7.83) * mm, v(-7.12, 8.99) * mm, v(-8, 9.76) * mm, v(-8.76, 10.53) * mm, v(-9.36, 11.47) * mm, v(-10.1, 12.24) * mm, v(-11.14, 12.84) * mm]});
            skSolve(sketch);
        }
        {
            var Q0;
            Q0=makeQuery(id+"F0.imprint","IMPRINT",FACE,{"disambiguationData":[TD([[makeQuery(id+"F0.imprint","IMPRINT",EDGE,{"derivedFrom":sQuery(id+"F0.wireOp",EDGE,"E0")}),1.0]])]});
            extrude(context, id + "F2", {"entities" : qUnion([Q0]), "oppositeDirection" : true, "depth" : 5.08 * mm, "offsetDistance" : 25.4 * mm});
        }
        {
            var Q0;
            Q0 = qSketchRegion(id + "F1", true);
            extrude(context, id + "F3", {"entities" : qUnion([Q0]), "operationType" : NewBodyOperationType.REMOVE, "endBound" : BoundingType.SYMMETRIC, "oppositeDirection" : true, "depth" : 2.54 * mm, "offsetDistance" : 25.4 * mm});
        }
        {
            var Q0;
            Q0=makeQuery(id+"F2.opExtrude","CAP_EDGE",EDGE,{"disambiguationData":[OSD([sQuery(id+"F0.wireOp",EDGE,"E37")])],"isStart":true});
            fillet(context, id + "F4", {"entities" : qUnion([Q0]), "radius" : 3.8 * mm, "tangentPropagation" : true, "allowEdgeOverflow" : false});
        }
    });
